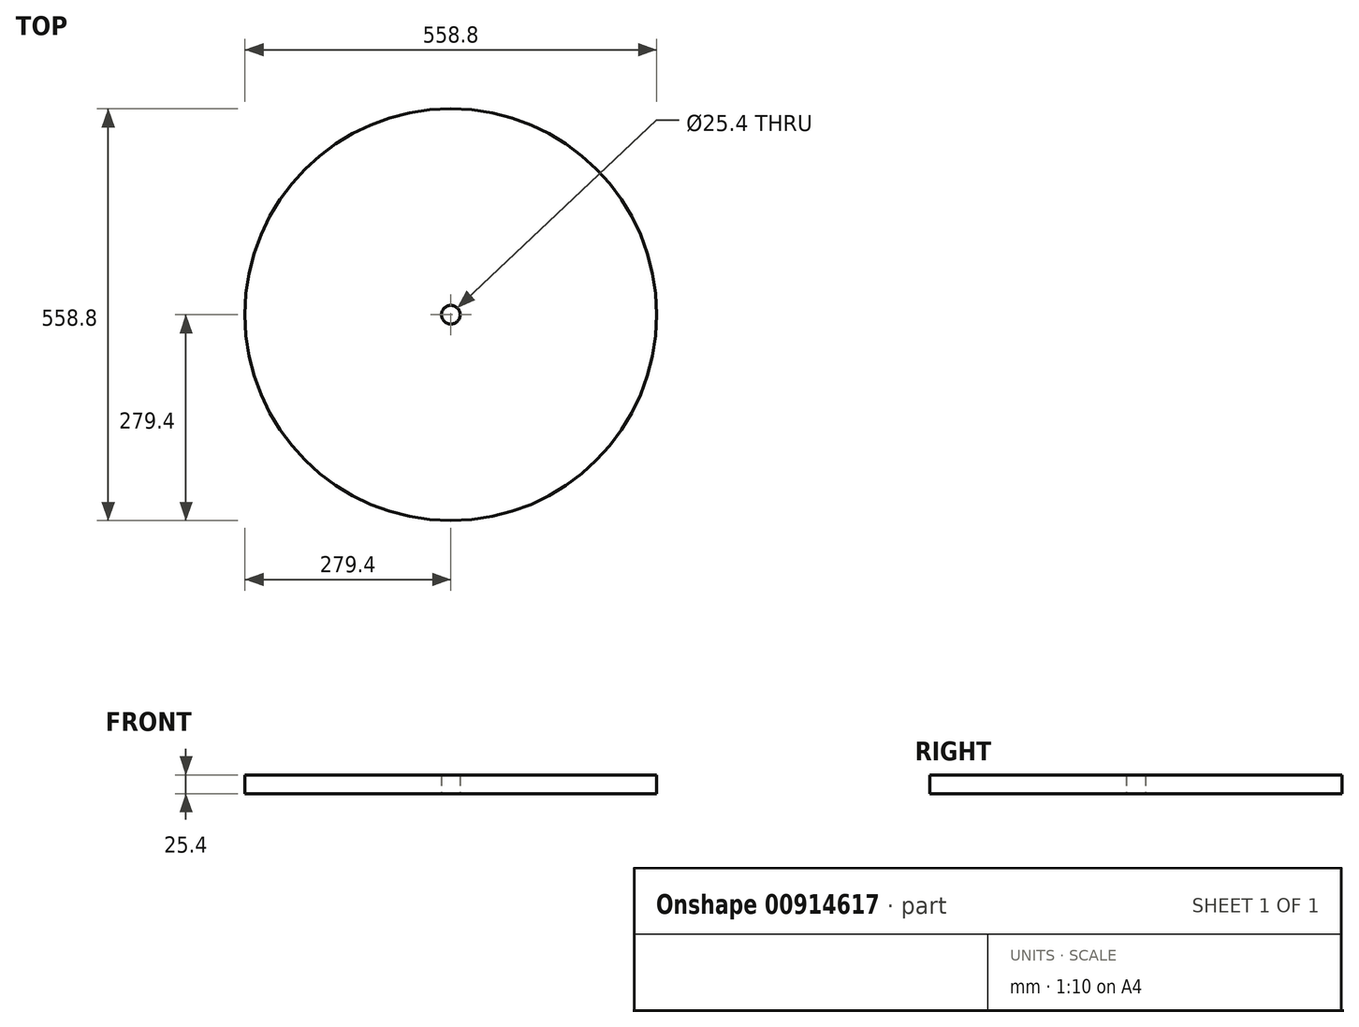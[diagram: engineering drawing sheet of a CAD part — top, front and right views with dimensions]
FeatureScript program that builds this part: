
annotation { "Feature Type Name" : "Feature", "Feature Type Description" : "" }
export const myFeature = defineFeature(function(context is Context, id is Id, definition is map)
    precondition{}
    {
        {
            var Q0;
            Q0=qCreatedBy(makeId("Top.planeOp"),FACE);
            var sketch = newSketch(context, id + "F0", { "sketchPlane" : qUnion([Q0])});
            skCircle(sketch, "E0", {"center": v(0, 0) * mm, "radius": 279.4 * mm});
            skCircle(sketch, "E1", {"center": v(0, 0) * mm, "radius": 12.7 * mm});
            skSolve(sketch);
        }
        {
            var Q0;
            Q0 = qSketchRegion(id + "F0", true);
            extrude(context, id + "F1", {"entities" : qUnion([Q0]), "depth" : 25.4 * mm, "offsetDistance" : 25.4 * mm});
        }
    });
